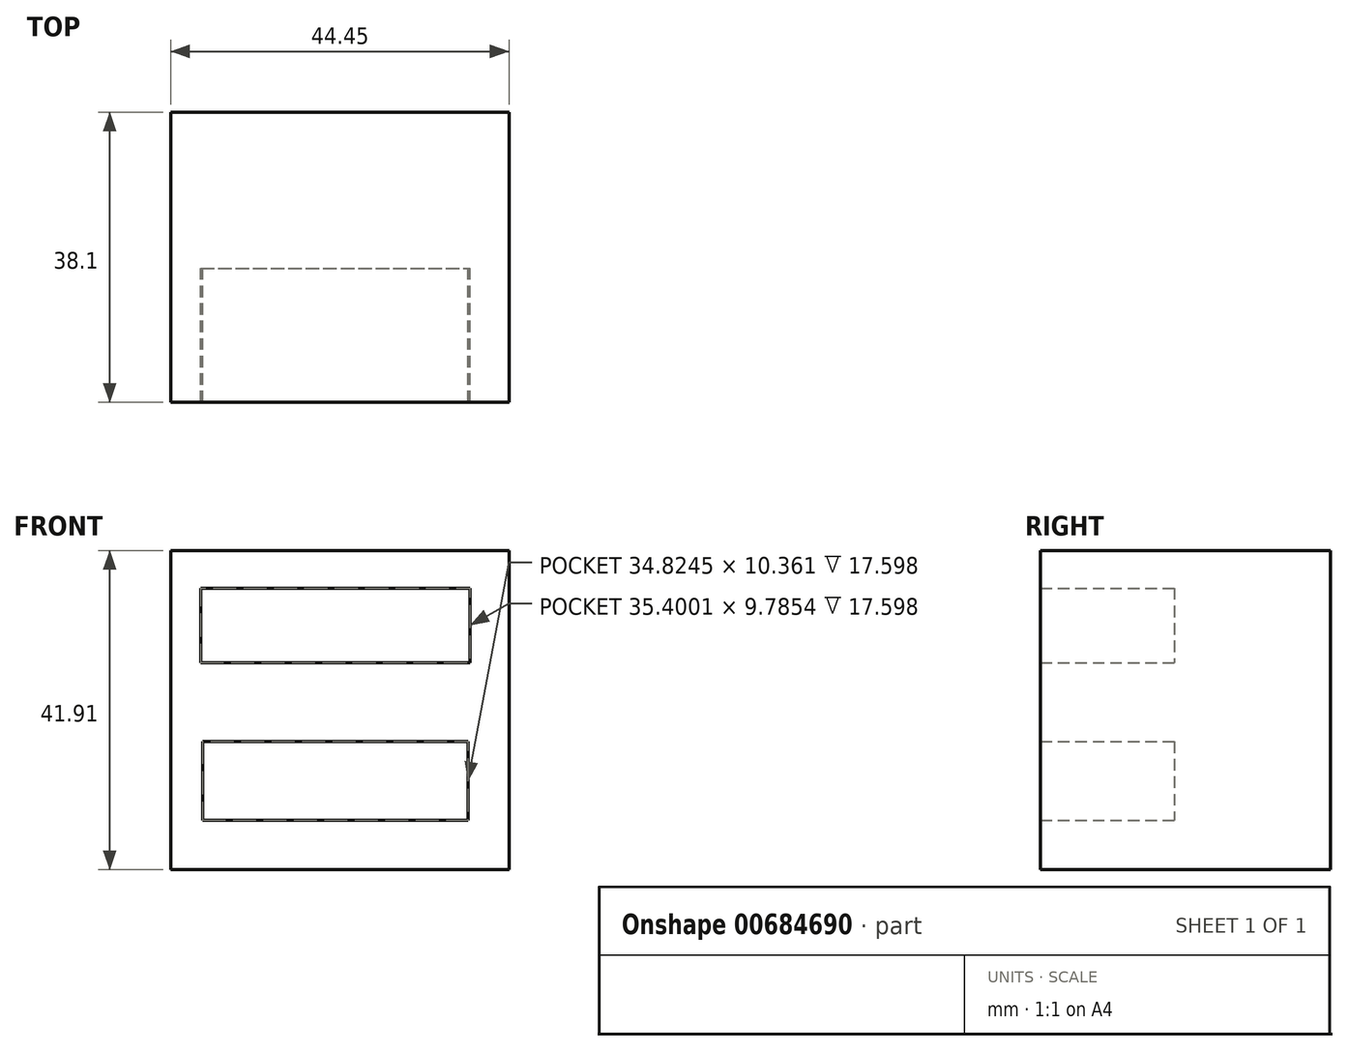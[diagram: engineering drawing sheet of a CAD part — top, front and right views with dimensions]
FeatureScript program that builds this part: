
annotation { "Feature Type Name" : "Feature", "Feature Type Description" : "" }
export const myFeature = defineFeature(function(context is Context, id is Id, definition is map)
    precondition{}
    {
        {
            var Q0;
            Q0=qCreatedBy(makeId("Top.planeOp"),FACE);
            var sketch = newSketch(context, id + "F0", { "sketchPlane" : qUnion([Q0])});
            skLineSegment(sketch, "E0.bottom", {"start": v(-18.2, 20.5) * mm, "end": v(26.26, 20.5) * mm});
            skLineSegment(sketch, "E0.top", {"start": v(-18.2, -17.6) * mm, "end": v(26.26, -17.6) * mm});
            skLineSegment(sketch, "E0.left", {"start": v(-18.2, 20.5) * mm, "end": v(-18.2, -17.6) * mm});
            skLineSegment(sketch, "E0.right", {"start": v(26.26, 20.5) * mm, "end": v(26.26, -17.6) * mm});
            skSolve(sketch);
        }
        {
            var Q0;
            Q0=qSketchRegion(id+"F0",true);
            extrude(context, id + "F1", {"entities" : qUnion([Q0]), "depth" : 41.9 * mm, "offsetDistance" : 25.4 * mm});
        }
        {
            var Q0;
            Q0=qCreatedBy(makeId("Front.planeOp"),FACE);
            var sketch = newSketch(context, id + "F2", { "sketchPlane" : qUnion([Q0])});
            skLineSegment(sketch, "E1.bottom", {"start": v(-14.25, 36.98) * mm, "end": v(21.15, 36.98) * mm});
            skLineSegment(sketch, "E1.top", {"start": v(-14.25, 27.2) * mm, "end": v(21.15, 27.2) * mm});
            skLineSegment(sketch, "E1.left", {"start": v(-14.25, 36.98) * mm, "end": v(-14.25, 27.2) * mm});
            skLineSegment(sketch, "E1.right", {"start": v(21.15, 36.98) * mm, "end": v(21.15, 27.2) * mm});
            skLineSegment(sketch, "E2.bottom", {"start": v(-13.96, 16.84) * mm, "end": v(20.87, 16.84) * mm});
            skLineSegment(sketch, "E2.top", {"start": v(-13.96, 6.48) * mm, "end": v(20.87, 6.48) * mm});
            skLineSegment(sketch, "E2.left", {"start": v(-13.96, 16.84) * mm, "end": v(-13.96, 6.48) * mm});
            skLineSegment(sketch, "E2.right", {"start": v(20.87, 16.84) * mm, "end": v(20.87, 6.48) * mm});
            skSolve(sketch);
        }
        {
            var Q0;
            Q0=qSketchRegion(id+"F2",true);
            extrude(context, id + "F3", {"entities" : qUnion([Q0]), "operationType" : NewBodyOperationType.REMOVE, "depth" : 19.05 * mm, "offsetDistance" : 25.4 * mm});
        }
    });
